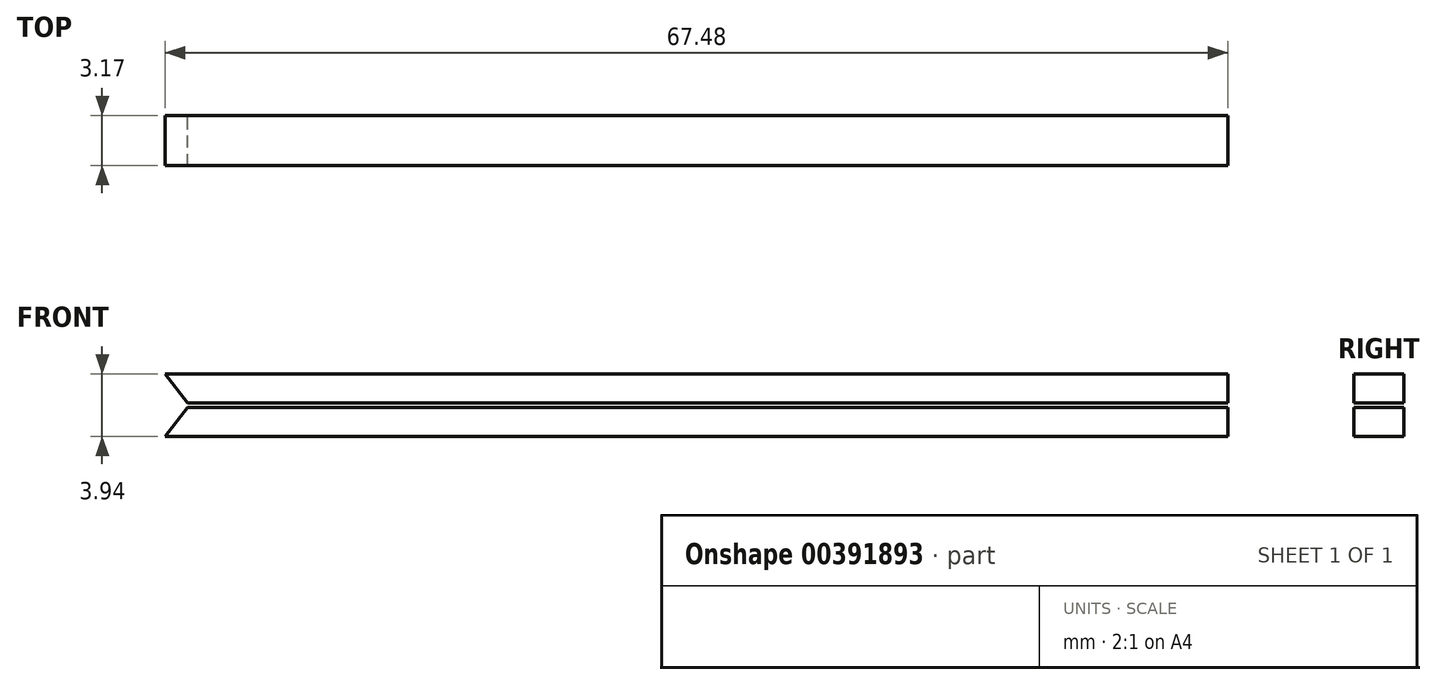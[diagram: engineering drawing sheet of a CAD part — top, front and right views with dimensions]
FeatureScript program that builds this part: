
annotation { "Feature Type Name" : "Feature", "Feature Type Description" : "" }
export const myFeature = defineFeature(function(context is Context, id is Id, definition is map)
    precondition{}
    {
        {
            var Q0;
            Q0=qCreatedBy(makeId("Front.planeOp"),FACE);
            var sketch = newSketch(context, id + "F0", { "sketchPlane" : qUnion([Q0])});
            skLineSegment(sketch, "E0", {"start": v(-13.67, -0.14) * mm, "end": v(-41.02, -0.14) * mm});
            skLineSegment(sketch, "E1", {"start": v(-41.02, -0.14) * mm, "end": v(-52.85, -0.14) * mm});
            skLineSegment(sketch, "E2", {"start": v(13.22, -0.14) * mm, "end": v(13.22, -1.97) * mm});
            skLineSegment(sketch, "E3", {"start": v(-13.67, -0.14) * mm, "end": v(-6.12, -0.14) * mm});
            skLineSegment(sketch, "E4", {"start": v(-6.12, -0.14) * mm, "end": v(13.22, -0.14) * mm});
            skLineSegment(sketch, "E5", {"start": v(-54.26, -1.97) * mm, "end": v(13.22, -1.97) * mm});
            skLineSegment(sketch, "E6", {"start": v(-52.85, -0.14) * mm, "end": v(-54.26, -1.97) * mm});
            skLineSegment(sketch, "E7.MirrorCS", {"start": v(-54.26, 1.97) * mm, "end": v(13.22, 1.97) * mm});
            skLineSegment(sketch, "E8.MirrorCS", {"start": v(-13.67, 0.14) * mm, "end": v(-41.02, 0.14) * mm});
            skLineSegment(sketch, "E9.MirrorCS", {"start": v(-13.67, 0.14) * mm, "end": v(-6.12, 0.14) * mm});
            skLineSegment(sketch, "E10.MirrorCS", {"start": v(-6.12, 0.14) * mm, "end": v(13.22, 0.14) * mm});
            skLineSegment(sketch, "E11.MirrorCS", {"start": v(13.22, 0.14) * mm, "end": v(13.22, 1.97) * mm});
            skLineSegment(sketch, "E12.MirrorCS", {"start": v(-52.85, 0.14) * mm, "end": v(-54.26, 1.97) * mm});
            skLineSegment(sketch, "E13.MirrorCS", {"start": v(-41.02, 0.14) * mm, "end": v(-52.85, 0.14) * mm});
            skSolve(sketch);
        }
        {
            var Q0;
            Q0=makeQuery(id+"F0.imprint","IMPRINT",FACE,{"disambiguationData":[TD([[makeQuery(id+"F0.imprint","IMPRINT",EDGE,{"derivedFrom":sQuery(id+"F0.wireOp",EDGE,"142a585d-a8d3-46f1-b98a-f50f8a6d9a05")}),1.0]])]});
            var Q1;
            Q1=makeQuery(id+"F0.imprint","IMPRINT",FACE,{"disambiguationData":[TD([[makeQuery(id+"F0.imprint","IMPRINT",EDGE,{"derivedFrom":sQuery(id+"F0.wireOp",EDGE,"E0")}),1.0]])]});
            var Q2;
            Q2=makeQuery(id+"F0.imprint","IMPRINT",FACE,{"disambiguationData":[TD([[makeQuery(id+"F0.imprint","IMPRINT",EDGE,{"derivedFrom":sQuery(id+"F0.wireOp",EDGE,"E7.MirrorCS")}),-1.0]])]});
            extrude(context, id + "F1", {"entities" : qUnion([Q0, Q1, Q2]), "depth" : 3.17 * mm});
        }
    });
